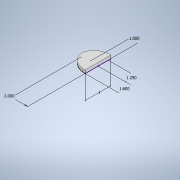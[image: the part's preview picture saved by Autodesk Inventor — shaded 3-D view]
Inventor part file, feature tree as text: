
AUTODESK INVENTOR PART (.ipt)
format: ipt  version: 2021 (Build 250183000, 183)  size: 126,464 bytes
history: native  units: in
note: dims shown in document units (in); Inventor stores cm internally (conversion verified against a paired STEP export)
features: extrude x3, other x2, sketch x2, projected_geometry x1
ambient origin geometry x8: Origin, YZ Plane, XZ Plane, XY Plane, X Axis, Y Axis, Z Axis, Center Point
bodies: Solid1 (feature_tree)
feature tree (8):
  other  "Annotations"
  sketch  "Sketch1"  dims[d0=2.0in d1=1.6in]
  extrude  "Extrusion1"  Depth=1.6in
  extrude  "Extrusion2"  Depth=1.25in
  extrude  "Extrusion3"  Depth=0.375in TaperAngle=0.0deg
  sketch  "Sketch3"  dims[d2=1.0in d3=1.25in d4=0.375in d5=0.0in d6=0.375in d7=0.0in d8=0.375in d9=0.375in d10=0.0in d16=3.2in]
  projected_geometry  "Projected Loop1"
  other  "Linear Dimension 1"
